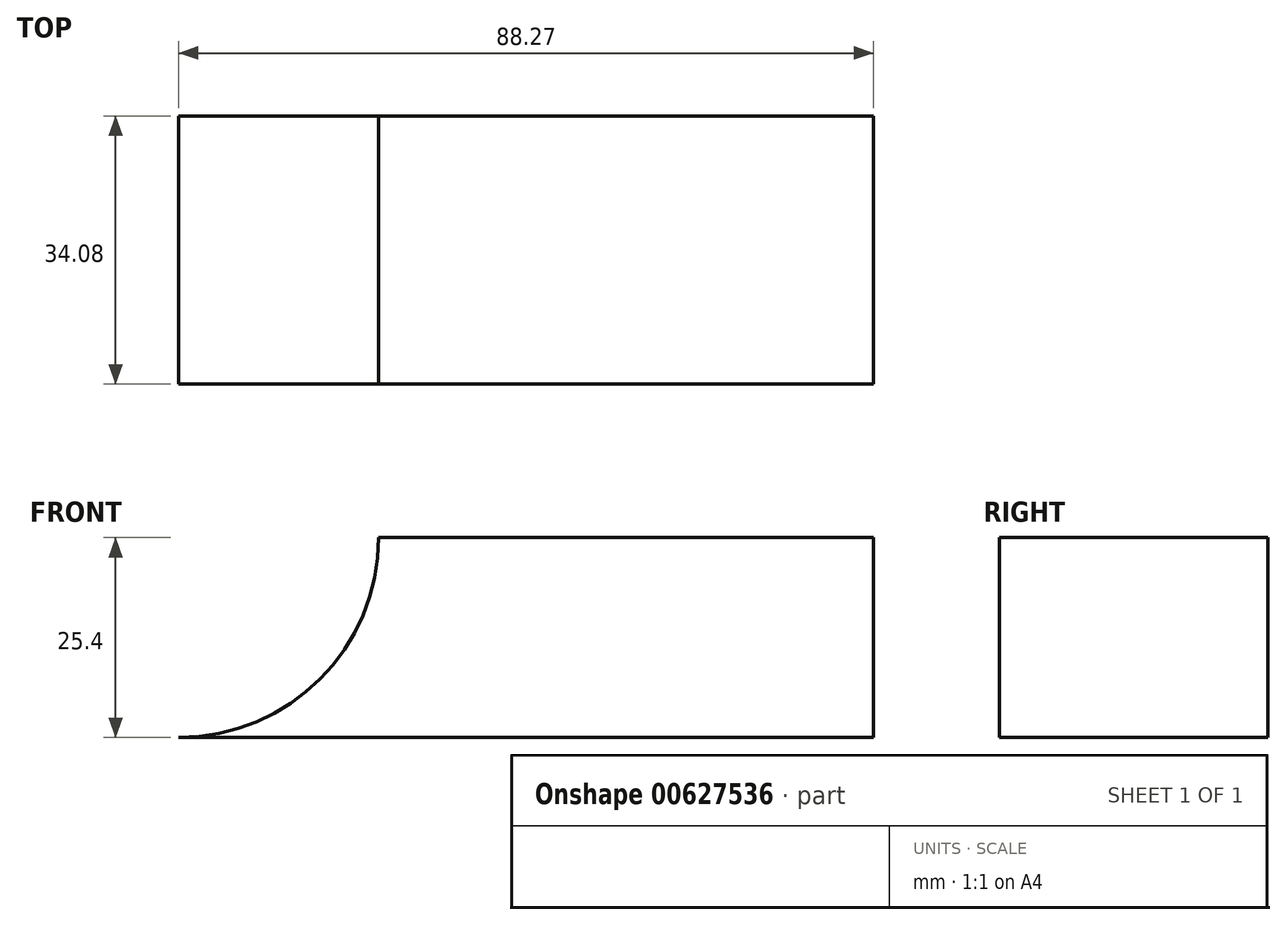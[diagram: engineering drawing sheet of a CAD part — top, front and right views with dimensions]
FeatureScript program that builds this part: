
annotation { "Feature Type Name" : "Feature", "Feature Type Description" : "" }
export const myFeature = defineFeature(function(context is Context, id is Id, definition is map)
    precondition{}
    {
        {
            var Q0;
            Q0=qCreatedBy(makeId("Top.planeOp"),FACE);
            var sketch = newSketch(context, id + "F0", { "sketchPlane" : qUnion([Q0])});
            skLineSegment(sketch, "E0.bottom", {"start": v(0, 0) * mm, "end": v(20.63, 0) * mm});
            skLineSegment(sketch, "E0.top", {"start": v(0, -34.08) * mm, "end": v(20.63, -34.08) * mm});
            skLineSegment(sketch, "E0.left", {"start": v(0, 0) * mm, "end": v(0, -34.08) * mm});
            skLineSegment(sketch, "E0.right", {"start": v(20.63, 0) * mm, "end": v(20.63, -34.08) * mm});
            skSolve(sketch);
        }
        {
            var Q0;
            Q0=sQuery(id+"F0.wireOp",EDGE,"E0.top");
            var Q1;
            Q1=sQuery(id+"F0.wireOp",EDGE,"E0.left");
            var Q2;
            Q2=sQuery(id+"F0.wireOp",EDGE,"E0.right");
            var Q3;
            Q3=sQuery(id+"F0.wireOp",EDGE,"E0.bottom");
            extrude(context, id + "F1", {"bodyType" : ToolBodyType.SURFACE, "surfaceEntities" : qUnion([Q0, Q1, Q2, Q3]), "depth" : 25.4 * mm, "offsetDistance" : 25.4 * mm});
        }
        {
            var Q0;
            Q0=makeQuery(id+"F1.opExtrude","SWEPT_FACE",FACE,{"disambiguationData":[OSD([sQuery(id+"F0.wireOp",EDGE,"E0.right")])]});
            extrude(context, id + "F2", {"entities" : qUnion([Q0]), "depth" : 88.26 * mm, "offsetDistance" : 25.4 * mm});
        }
        {
            var Q0;
            Q0=makeQuery(id+"F1.opExtrude","SWEPT_FACE",FACE,{"disambiguationData":[OSD([sQuery(id+"F0.wireOp",EDGE,"E0.right")])]});
            var Q1;
            Q1=makeQuery(id+"F1.opExtrude","CAP_EDGE",EDGE,{"disambiguationData":[OSD([sQuery(id+"F0.wireOp",EDGE,"E0.right")])],"isStart":false});
            revolve(context, id + "F3", {"operationType" : NewBodyOperationType.REMOVE, "entities" : qUnion([Q0]), "axis" : qUnion([Q1]), "revolveType" : RevolveType.FULL, "oppositeDirection" : true});
        }
    });
